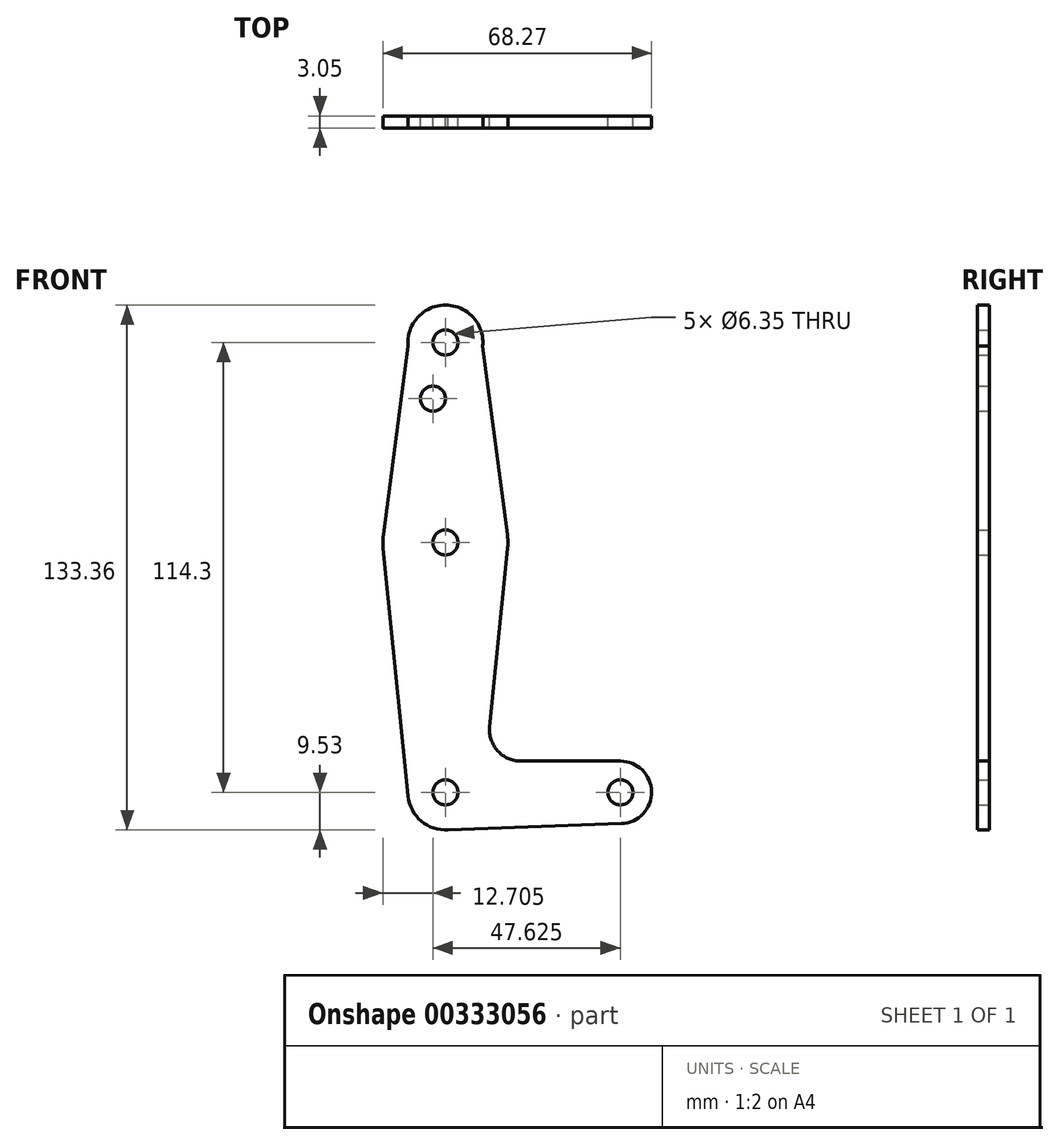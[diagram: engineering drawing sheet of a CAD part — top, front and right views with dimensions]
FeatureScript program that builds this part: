
annotation { "Feature Type Name" : "Feature", "Feature Type Description" : "" }
export const myFeature = defineFeature(function(context is Context, id is Id, definition is map)
    precondition{}
    {
        {
            var Q0;
            Q0=qCreatedBy(makeId("Front.planeOp"),FACE);
            var sketch = newSketch(context, id + "F0", { "sketchPlane" : qUnion([Q0])});
            skCircle(sketch, "E0", {"center": v(0, 0) * mm, "radius": 9.53 * mm});
            skLineSegment(sketch, "E1", {"start": v(0, 0) * mm, "end": v(0, 114.3) * mm, "construction": true});
            skLineSegment(sketch, "E2", {"start": v(0, 0) * mm, "end": v(44.45, 0) * mm, "construction": true});
            skCircle(sketch, "E3", {"center": v(0, 114.3) * mm, "radius": 9.53 * mm});
            skCircle(sketch, "E4", {"center": v(44.45, 0) * mm, "radius": 7.94 * mm});
            skCircle(sketch, "E5", {"center": v(0, 63.5) * mm, "radius": 15.88 * mm});
            skLineSegment(sketch, "E6", {"start": v(-15.74, 65.56) * mm, "end": v(-9.48, 113.35) * mm});
            skLineSegment(sketch, "E7", {"start": v(9.48, 113.35) * mm, "end": v(15.74, 65.56) * mm});
            skLineSegment(sketch, "E8", {"start": v(-9.48, -0.95) * mm, "end": v(-15.8, 61.91) * mm});
            skLineSegment(sketch, "E9", {"start": v(44.45, 7.94) * mm, "end": v(19.16, 7.94) * mm});
            skCircle(sketch, "E10", {"center": v(0, 114.3) * mm, "radius": 3.18 * mm});
            skCircle(sketch, "E11", {"center": v(0, 63.5) * mm, "radius": 3.18 * mm});
            skCircle(sketch, "E12", {"center": v(0, 0) * mm, "radius": 3.18 * mm});
            skCircle(sketch, "E13", {"center": v(44.45, 0) * mm, "radius": 3.18 * mm});
            skCircle(sketch, "E14", {"center": v(-3.17, 100.03) * mm, "radius": 3.18 * mm});
            skLineSegment(sketch, "E15", {"start": v(15.8, 61.91) * mm, "end": v(11.25, 16.68) * mm});
            skArc(sketch, "E16.filletArc", {"start": v(11.25, 16.68) * mm, "mid": v(13.26, 10.55) * mm, "end": v(19.16, 7.94) * mm});
            skLineSegment(sketch, "E17", {"start": v(0, -9.53) * mm, "end": v(44.73, -7.93) * mm});
            skSolve(sketch);
        }
        {
            var Q0;
            Q0 = qSketchRegion(id + "F0", true);
            extrude(context, id + "F1", {"entities" : qUnion([Q0]), "depth" : 3.05 * mm});
        }
    });
